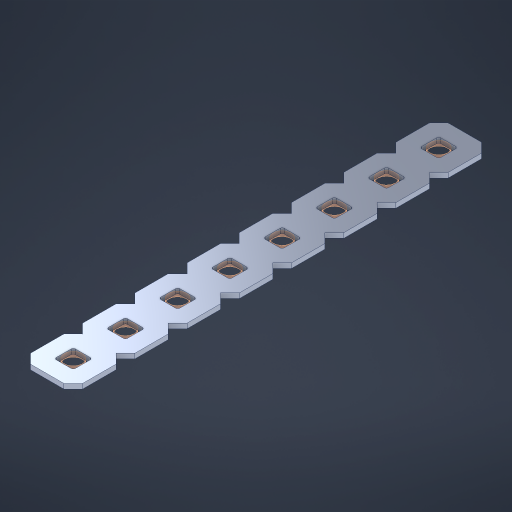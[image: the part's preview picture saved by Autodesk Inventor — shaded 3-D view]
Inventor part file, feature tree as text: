
AUTODESK INVENTOR PART (.ipt)
format: ipt  version: 2023 (Build 270158000, 158)  size: 363,008 bytes
history: native  units: in
note: dims shown in document units (in); Inventor stores cm internally (conversion verified against a paired STEP export)
features: other x9, extrude x7, sketch x2, pattern_linear x1
ambient origin geometry x8: Origin, YZ Plane, XZ Plane, XY Plane, X Axis, Y Axis, Z Axis, Center Point
bodies: Solid1 (feature_tree), Body (feature_tree)
feature tree (19):
  pattern_linear  "Rectangular Pattern1"  Spacing1=0.09in  [1 undecoded]
  sketch  "Sketch1"  dims[d1=0.5in]
  sketch  "Sketch2"  dims[d2=0.182in d3=0.09in d4=0.09in d5=0.09in d6=0.09in d7=0.09in d8=0.09in d9=0.09in d10=0.09in d11=0.02in d13=0.0in d14=0.172in d15=0.0625in d16=0.0in d19=0.5in d22=0.5in]
  other  "Srf1"
  other  "Srf126"
  other  "Srf127"
  other  "Srf128"
  other  "Srf129"
  other  "Srf130"
  other  "Srf131"
  other  "Srf250"
  other  "Circle"
  extrude  "ExtrusionSrf126"  Depth=0.09in
  extrude  "ExtrusionSrf127"  Depth=0.09in
  extrude  "ExtrusionSrf128"  Depth=0.09in
  extrude  "ExtrusionSrf129"  Depth=0.09in
  extrude  "ExtrusionSrf130"  Depth=0.09in
  extrude  "ExtrusionSrf131"  Depth=0.09in
  extrude  "ExtrusionSrf250"  Depth=0.09in
note: 1 required parameter value undecoded (feature->parameter linkage not recoverable at this tier; creation-order binding heuristic only, values carry confidence <= 0.55)
